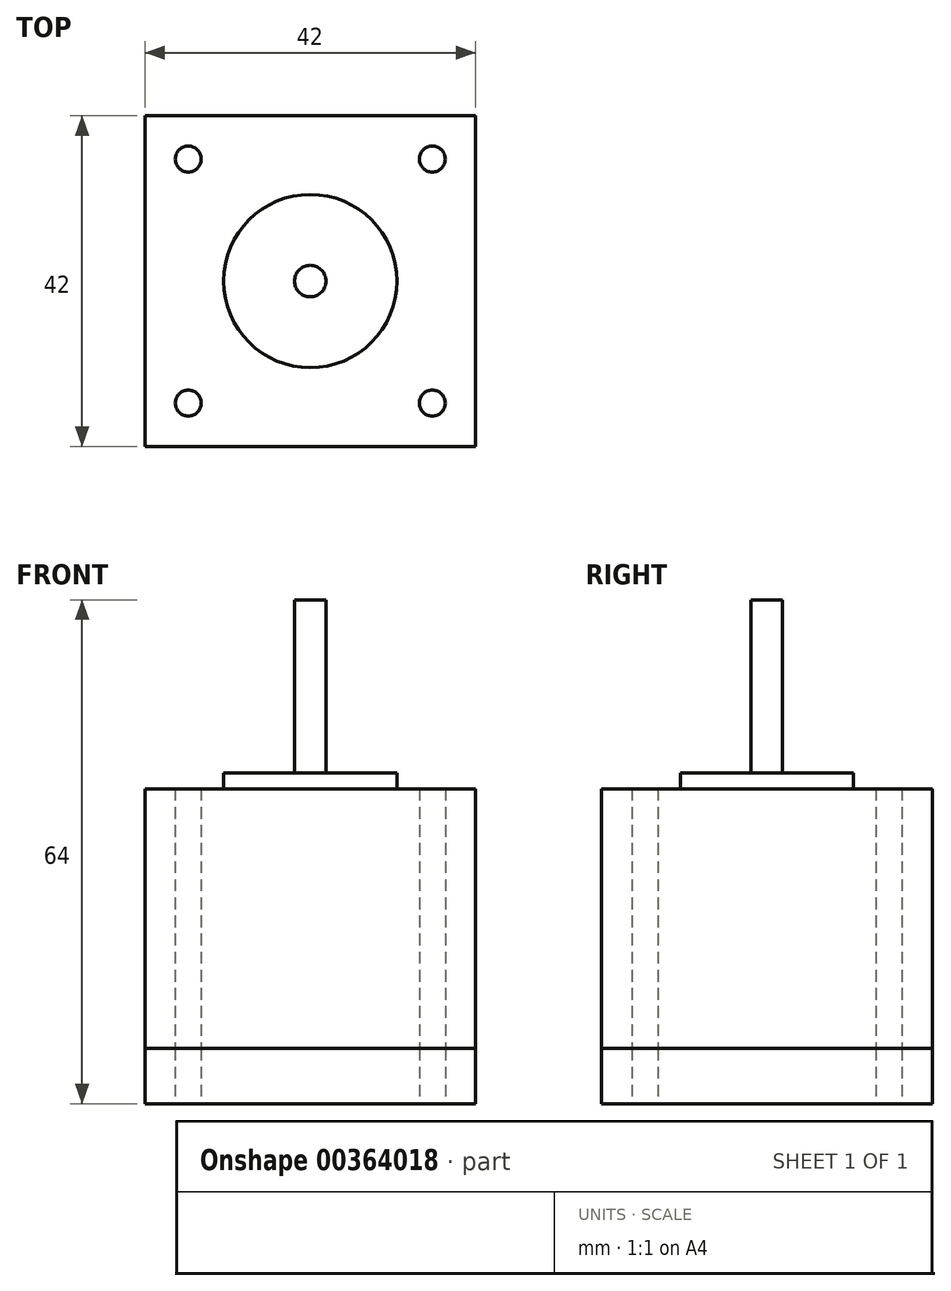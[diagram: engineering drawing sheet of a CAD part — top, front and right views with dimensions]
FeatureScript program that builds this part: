
annotation { "Feature Type Name" : "Feature", "Feature Type Description" : "" }
export const myFeature = defineFeature(function(context is Context, id is Id, definition is map)
    precondition{}
    {
        {
            var Q0;
            Q0=qCreatedBy(makeId("Top.planeOp"),FACE);
            var sketch = newSketch(context, id + "F0", { "sketchPlane" : qUnion([Q0])});
            skLineSegment(sketch, "E0.bottom", {"start": v(21, -21) * mm, "end": v(-21, -21) * mm});
            skLineSegment(sketch, "E0.top", {"start": v(21, 21) * mm, "end": v(-21, 21) * mm});
            skLineSegment(sketch, "E0.left", {"start": v(21, -21) * mm, "end": v(21, 21) * mm});
            skLineSegment(sketch, "E0.right", {"start": v(-21, -21) * mm, "end": v(-21, 21) * mm});
            skPoint(sketch, "E0.middle", {"position": v(0, 0) * mm});
            skSolve(sketch);
        }
        {
            var Q0;
            Q0=makeQuery(id+"F0.imprint","IMPRINT",FACE,{"disambiguationData":[TD([[makeQuery(id+"F0.imprint","IMPRINT",EDGE,{"derivedFrom":sQuery(id+"F0.wireOp",EDGE,"E0.bottom")}),-1.0]])]});
            extrude(context, id + "F1", {"entities" : qUnion([Q0]), "depth" : 7 * mm});
        }
        {
            var Q0;
            Q0=makeQuery(id+"F1.opExtrude","CAP_FACE",FACE,{"disambiguationData":[OSD([sQuery(id+"F0.wireOp",EDGE,"E0.bottom"),sQuery(id+"F0.wireOp",EDGE,"E0.top"),sQuery(id+"F0.wireOp",EDGE,"E0.left"),sQuery(id+"F0.wireOp",EDGE,"E0.right")])],"isStart":false});
            extrude(context, id + "F2", {"entities" : qUnion([Q0]), "depth" : 26 * mm});
        }
        {
            var Q0;
            Q0=makeQuery(id+"F2.opExtrude","CAP_FACE",FACE,{"disambiguationData":[OSD([sQuery(id+"F0.wireOp",EDGE,"E0.bottom"),sQuery(id+"F0.wireOp",EDGE,"E0.top"),sQuery(id+"F0.wireOp",EDGE,"E0.left"),sQuery(id+"F0.wireOp",EDGE,"E0.right")])],"isStart":false});
            extrude(context, id + "F3", {"entities" : qUnion([Q0]), "operationType" : NewBodyOperationType.ADD, "depth" : 7 * mm});
        }
        {
            var Q0;
            Q0=makeQuery(id+"F3.opExtrude","CAP_FACE",FACE,{"disambiguationData":[OSD([sQuery(id+"F0.wireOp",EDGE,"E0.bottom"),sQuery(id+"F0.wireOp",EDGE,"E0.top"),sQuery(id+"F0.wireOp",EDGE,"E0.left"),sQuery(id+"F0.wireOp",EDGE,"E0.right")])],"isStart":false});
            var sketch = newSketch(context, id + "F4", { "sketchPlane" : qUnion([Q0])});
            skPoint(sketch, "E1", {"position": v(-15.5, 15.5) * mm});
            skPoint(sketch, "E2.0.1.0", {"position": v(-15.5, -15.5) * mm});
            skPoint(sketch, "E2.1.0.0", {"position": v(15.5, 15.5) * mm});
            skPoint(sketch, "E2.1.1.0", {"position": v(15.5, -15.5) * mm});
            skLineSegment(sketch, "E2.direction1", {"start": v(-15.5, 15.5) * mm, "end": v(15.5, 15.5) * mm, "construction": true});
            skLineSegment(sketch, "E2.direction2", {"start": v(-15.5, 15.5) * mm, "end": v(-15.5, -15.5) * mm, "construction": true});
            skSolve(sketch);
        }
        {
            var Q0;
            Q0=sQuery(id+"F4.wireOp",VERTEX,"E1");
            var Q1;
            Q1=sQuery(id+"F4.wireOp",VERTEX,"E2.1.0.0");
            var Q2;
            Q2=sQuery(id+"F4.wireOp",VERTEX,"E2.0.1.0");
            var Q3;
            Q3=sQuery(id+"F4.wireOp",VERTEX,"E2.1.1.0");
            var Q4;
            Q4=makeQuery(id+"F1.opExtrude","SWEPT_BODY",BODY,{"disambiguationData":[OSD([sQuery(id+"F0.wireOp",EDGE,"E0.bottom"),sQuery(id+"F0.wireOp",EDGE,"E0.top"),sQuery(id+"F0.wireOp",EDGE,"E0.left"),sQuery(id+"F0.wireOp",EDGE,"E0.right")])]});
            var Q5;
            Q5=makeQuery(id+"F3.opExtrude","SWEPT_BODY",BODY,{"disambiguationData":[OSD([sQuery(id+"F0.wireOp",EDGE,"E0.bottom"),sQuery(id+"F0.wireOp",EDGE,"E0.top"),sQuery(id+"F0.wireOp",EDGE,"E0.left"),sQuery(id+"F0.wireOp",EDGE,"E0.right")])]});
            var Q6;
            Q6=makeQuery(id+"F2.opExtrude","SWEPT_BODY",BODY,{"disambiguationData":[OSD([sQuery(id+"F0.wireOp",EDGE,"E0.bottom"),sQuery(id+"F0.wireOp",EDGE,"E0.top"),sQuery(id+"F0.wireOp",EDGE,"E0.left"),sQuery(id+"F0.wireOp",EDGE,"E0.right")])]});
            hole(context, id + "F5", {"style" : HoleStyle.SIMPLE, "endStyle" : HoleEndStyle.THROUGH, "standardTappedOrClearance" : lookupTablePath({ "standard" : "ISO", "fit" : "Normal", "size" : "M3", "type" : "Clearance" }), "standardBlindInLast" : lookupTablePath({ "fit" : "Standard", "standard" : "ISO", "size" : "M3", "type" : "Clearance" }), "holeDiameter" : 3.3 * mm, "isTappedThrough" : true, "tappedDepth" : 12 * mm, "tapClearance" : 3, "locations" : qUnion([Q0, Q1, Q2, Q3]), "scope" : qUnion([Q4, Q5, Q6]), "startStyle" : HoleStartStyle.PART});
        }
        {
            var Q0;
            Q0=makeQuery(id+"F3.opExtrude","CAP_FACE",FACE,{"disambiguationData":[OSD([sQuery(id+"F0.wireOp",EDGE,"E0.bottom"),sQuery(id+"F0.wireOp",EDGE,"E0.top"),sQuery(id+"F0.wireOp",EDGE,"E0.left"),sQuery(id+"F0.wireOp",EDGE,"E0.right")])],"isStart":false});
            var sketch = newSketch(context, id + "F6", { "sketchPlane" : qUnion([Q0])});
            skCircle(sketch, "E3", {"center": v(0, 0) * mm, "radius": 11 * mm});
            skSolve(sketch);
        }
        {
            var Q0;
            Q0=makeQuery(id+"F6.imprint","IMPRINT",FACE,{"disambiguationData":[TD([[makeQuery(id+"F6.imprint","IMPRINT",EDGE,{"derivedFrom":sQuery(id+"F6.wireOp",EDGE,"E3")}),1.0]])]});
            extrude(context, id + "F7", {"entities" : qUnion([Q0]), "operationType" : NewBodyOperationType.ADD, "depth" : 2 * mm});
        }
        {
            var Q0;
            Q0=makeQuery(id+"F7.opExtrude","CAP_FACE",FACE,{"disambiguationData":[OSD([sQuery(id+"F6.wireOp",EDGE,"E3")])],"isStart":false});
            var sketch = newSketch(context, id + "F8", { "sketchPlane" : qUnion([Q0])});
            skCircle(sketch, "E4", {"center": v(0, 0) * mm, "radius": 2 * mm});
            skSolve(sketch);
        }
        {
            var Q0;
            Q0=qSketchRegion(id+"F8",true);
            extrude(context, id + "F9", {"entities" : qUnion([Q0]), "operationType" : NewBodyOperationType.ADD, "depth" : 22 * mm});
        }
    });
